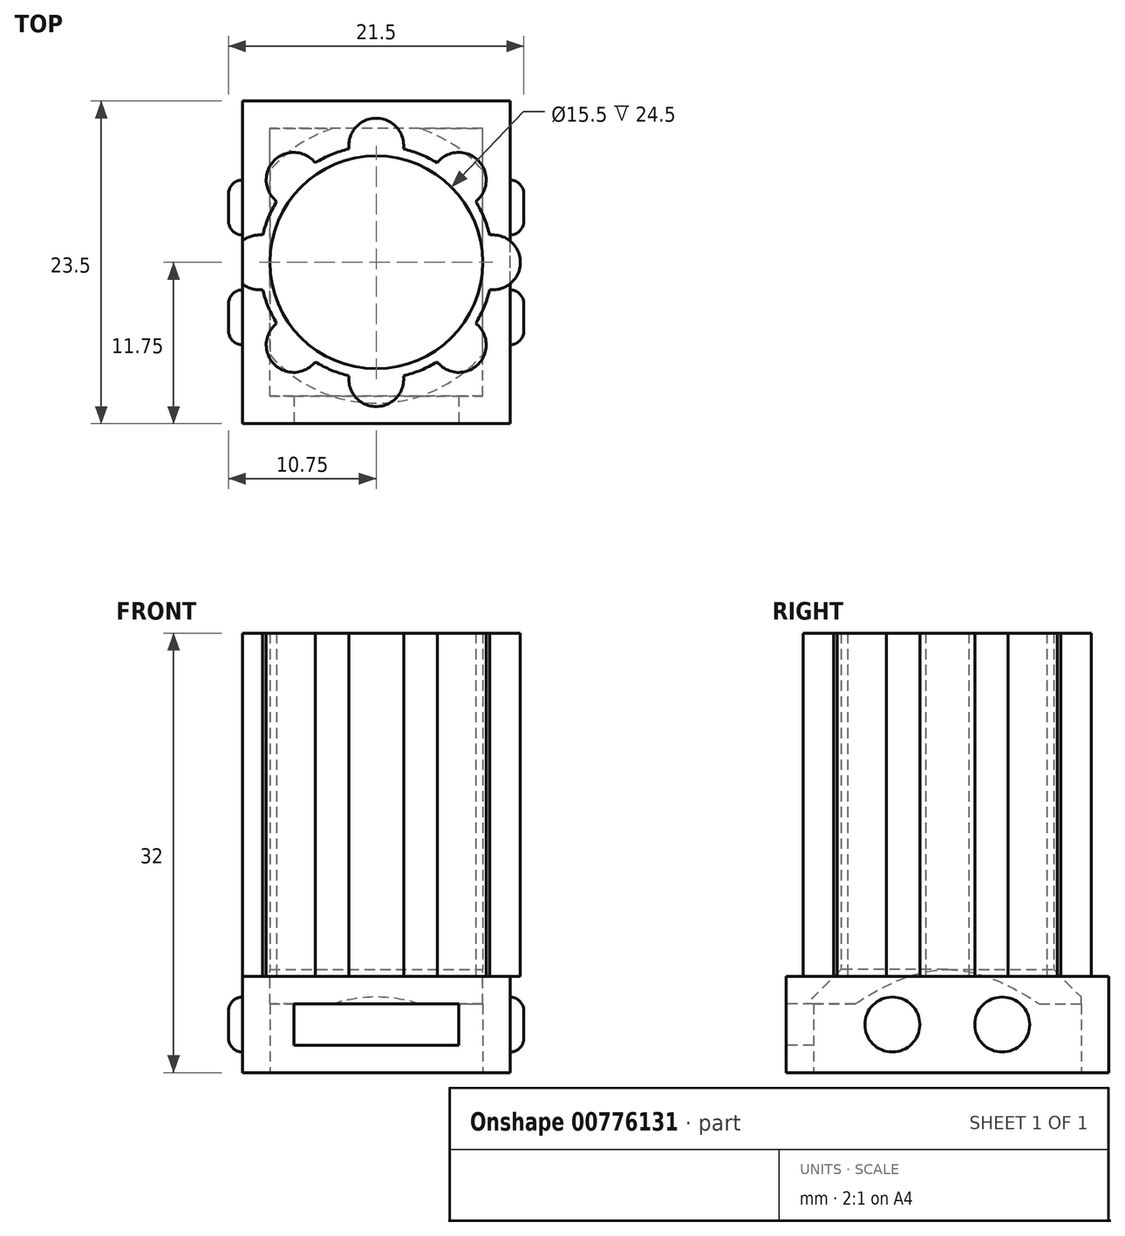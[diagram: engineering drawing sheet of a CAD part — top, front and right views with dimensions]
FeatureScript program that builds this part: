
annotation { "Feature Type Name" : "Feature", "Feature Type Description" : "" }
export const myFeature = defineFeature(function(context is Context, id is Id, definition is map)
    precondition{}
    {
        {
            var Q0;
            Q0=qCreatedBy(makeId("Top.planeOp"),FACE);
            var sketch = newSketch(context, id + "F0", { "sketchPlane" : qUnion([Q0])});
            skLineSegment(sketch, "E0.bottom", {"start": v(9.75, -11.75) * mm, "end": v(-9.75, -11.75) * mm});
            skLineSegment(sketch, "E0.top", {"start": v(9.75, 11.75) * mm, "end": v(-9.75, 11.75) * mm});
            skLineSegment(sketch, "E0.left", {"start": v(9.75, -11.75) * mm, "end": v(9.75, 11.75) * mm});
            skLineSegment(sketch, "E0.right", {"start": v(-9.75, -11.75) * mm, "end": v(-9.75, 11.75) * mm});
            skPoint(sketch, "E0.middle", {"position": v(0, 0) * mm});
            skLineSegment(sketch, "E1.bottom", {"start": v(7.75, -9.75) * mm, "end": v(-7.75, -9.75) * mm});
            skLineSegment(sketch, "E1.top", {"start": v(7.75, 9.75) * mm, "end": v(-7.75, 9.75) * mm});
            skLineSegment(sketch, "E1.left", {"start": v(7.75, -9.75) * mm, "end": v(7.75, 9.75) * mm});
            skLineSegment(sketch, "E1.right", {"start": v(-7.75, -9.75) * mm, "end": v(-7.75, 9.75) * mm});
            skSolve(sketch);
        }
        {
            var Q0;
            Q0=makeQuery(id+"F0.imprint","IMPRINT",FACE,{"disambiguationData":[TD([[makeQuery(id+"F0.imprint","IMPRINT",EDGE,{"derivedFrom":sQuery(id+"F0.wireOp",EDGE,"E0.bottom")}),-1.0]])]});
            extrude(context, id + "F1", {"entities" : qUnion([Q0]), "depth" : 7 * mm, "offsetDistance" : 25 * mm});
        }
        {
            var Q0;
            Q0=makeQuery(id+"F1.opExtrude","SWEPT_FACE",FACE,{"disambiguationData":[OSD([sQuery(id+"F0.wireOp",EDGE,"E0.left")])]});
            var sketch = newSketch(context, id + "F2", { "sketchPlane" : qUnion([Q0])});
            skPoint(sketch, "E2", {"position": v(0, 0) * mm});
            skPoint(sketch, "E3", {"position": v(0, 3.5) * mm});
            skPoint(sketch, "E4", {"position": v(4, 3.5) * mm});
            skPoint(sketch, "E5", {"position": v(-4, 3.5) * mm});
            skCircle(sketch, "E6", {"center": v(4, 3.5) * mm, "radius": 2 * mm});
            skCircle(sketch, "E7", {"center": v(-4, 3.5) * mm, "radius": 2 * mm});
            skSolve(sketch);
        }
        {
            var Q0;
            Q0=makeQuery(id+"F2.imprint","IMPRINT",FACE,{"disambiguationData":[TD([[makeQuery(id+"F2.imprint","IMPRINT",EDGE,{"derivedFrom":sQuery(id+"F2.wireOp",EDGE,"E7")}),1.0]])]});
            var Q1;
            Q1=makeQuery(id+"F2.imprint","IMPRINT",FACE,{"disambiguationData":[TD([[makeQuery(id+"F2.imprint","IMPRINT",EDGE,{"derivedFrom":sQuery(id+"F2.wireOp",EDGE,"E6")}),1.0]])]});
            extrude(context, id + "F3", {"entities" : qUnion([Q0, Q1]), "operationType" : NewBodyOperationType.ADD, "depth" : 1 * mm, "offsetDistance" : 25 * mm});
        }
        {
            var Q0;
            Q0=makeQuery(id+"F3.opExtrude","CAP_EDGE",EDGE,{"disambiguationData":[OSD([sQuery(id+"F2.wireOp",EDGE,"E6")])],"isStart":false});
            var Q1;
            Q1=makeQuery(id+"F3.opExtrude","CAP_EDGE",EDGE,{"disambiguationData":[OSD([sQuery(id+"F2.wireOp",EDGE,"E7")])],"isStart":false});
            fillet(context, id + "F4", {"entities" : qUnion([Q0, Q1]), "radius" : 1 * mm, "tangentPropagation" : true, "allowEdgeOverflow" : false});
        }
        {
            var Q0;
            Q0=makeQuery(id+"F1.opExtrude","SWEPT_FACE",FACE,{"disambiguationData":[OSD([sQuery(id+"F0.wireOp",EDGE,"E0.right")])]});
            var sketch = newSketch(context, id + "F5", { "sketchPlane" : qUnion([Q0])});
            skPoint(sketch, "E8", {"position": v(0, 0) * mm});
            skPoint(sketch, "E9", {"position": v(0, 3.5) * mm});
            skPoint(sketch, "E10", {"position": v(4, 3.5) * mm});
            skPoint(sketch, "E11", {"position": v(-4, 3.5) * mm});
            skCircle(sketch, "E12", {"center": v(4, 3.5) * mm, "radius": 2 * mm});
            skCircle(sketch, "E13", {"center": v(-4, 3.5) * mm, "radius": 2 * mm});
            skSolve(sketch);
        }
        {
            var Q0;
            Q0=makeQuery(id+"F5.imprint","IMPRINT",FACE,{"disambiguationData":[TD([[makeQuery(id+"F5.imprint","IMPRINT",EDGE,{"derivedFrom":sQuery(id+"F5.wireOp",EDGE,"E12")}),1.0]])]});
            var Q1;
            Q1=makeQuery(id+"F5.imprint","IMPRINT",FACE,{"disambiguationData":[TD([[makeQuery(id+"F5.imprint","IMPRINT",EDGE,{"derivedFrom":sQuery(id+"F5.wireOp",EDGE,"E13")}),1.0]])]});
            extrude(context, id + "F6", {"entities" : qUnion([Q0, Q1]), "operationType" : NewBodyOperationType.ADD, "depth" : 1 * mm, "offsetDistance" : 25 * mm});
        }
        {
            var Q0;
            Q0=makeQuery(id+"F6.opExtrude","CAP_EDGE",EDGE,{"disambiguationData":[OSD([sQuery(id+"F5.wireOp",EDGE,"E12")])],"isStart":false});
            var Q1;
            Q1=makeQuery(id+"F6.opExtrude","CAP_EDGE",EDGE,{"disambiguationData":[OSD([sQuery(id+"F5.wireOp",EDGE,"E13")])],"isStart":false});
            fillet(context, id + "F7", {"entities" : qUnion([Q0, Q1]), "radius" : 1 * mm, "tangentPropagation" : true, "allowEdgeOverflow" : false});
        }
        {
            var Q0;
            Q0=makeQuery(id+"F1.opExtrude","SWEPT_FACE",FACE,{"disambiguationData":[OSD([sQuery(id+"F0.wireOp",EDGE,"E1.top")])]});
            var sketch = newSketch(context, id + "F8", { "sketchPlane" : qUnion([Q0])});
            skLineSegment(sketch, "E14.bottom", {"start": v(-7.75, 7) * mm, "end": v(7.75, 7) * mm});
            skLineSegment(sketch, "E14.top", {"start": v(-7.75, 5) * mm, "end": v(7.75, 5) * mm});
            skLineSegment(sketch, "E14.left", {"start": v(-7.75, 7) * mm, "end": v(-7.75, 5) * mm});
            skLineSegment(sketch, "E14.right", {"start": v(7.75, 7) * mm, "end": v(7.75, 5) * mm});
            skSolve(sketch);
        }
        {
            var Q0;
            Q0=makeQuery(id+"F8.imprint","IMPRINT",FACE,{"disambiguationData":[TD([[makeQuery(id+"F8.imprint","IMPRINT",EDGE,{"derivedFrom":sQuery(id+"F8.wireOp",EDGE,"E14.bottom")}),1.0]])]});
            extrude(context, id + "F9", {"entities" : qUnion([Q0]), "operationType" : NewBodyOperationType.ADD, "endBound" : BoundingType.UP_TO_NEXT, "depth" : 25 * mm, "offsetDistance" : 25 * mm});
        }
        {
            var Q0;
            Q0=makeQuery(id+"F9.boolean.opBoolean","MERGE",FACE,{"derivedFrom":[makeQuery(id+"F1.opExtrude","CAP_FACE",FACE,{"disambiguationData":[OSD([sQuery(id+"F0.wireOp",EDGE,"E0.bottom"),sQuery(id+"F0.wireOp",EDGE,"E0.top"),sQuery(id+"F0.wireOp",EDGE,"E0.left"),sQuery(id+"F0.wireOp",EDGE,"E0.right"),sQuery(id+"F0.wireOp",EDGE,"E1.bottom"),sQuery(id+"F0.wireOp",EDGE,"E1.top"),sQuery(id+"F0.wireOp",EDGE,"E1.left"),sQuery(id+"F0.wireOp",EDGE,"E1.right")])],"isStart":false}),makeQuery(id+"F9.opExtrude","SWEPT_FACE",FACE,{"disambiguationData":[OSD([sQuery(id+"F8.wireOp",EDGE,"E14.bottom")])]})]});
            var sketch = newSketch(context, id + "F10", { "sketchPlane" : qUnion([Q0])});
            skCircle(sketch, "E15", {"center": v(0, 0) * mm, "radius": 8.5 * mm});
            skCircle(sketch, "E16", {"center": v(0, 8.5) * mm, "radius": 2 * mm});
            skCircle(sketch, "E17.1.0", {"center": v(-6.01, 6.01) * mm, "radius": 2 * mm});
            skCircle(sketch, "E17.2.0", {"center": v(-8.5, 0) * mm, "radius": 2 * mm});
            skCircle(sketch, "E17.3.0", {"center": v(-6.01, -6.01) * mm, "radius": 2 * mm});
            skCircle(sketch, "E17.4.0", {"center": v(0, -8.5) * mm, "radius": 2 * mm});
            skCircle(sketch, "E17.5.0", {"center": v(6.01, -6.01) * mm, "radius": 2 * mm});
            skCircle(sketch, "E17.6.0", {"center": v(8.5, 0) * mm, "radius": 2 * mm});
            skCircle(sketch, "E17.7.0", {"center": v(6.01, 6.01) * mm, "radius": 2 * mm});
            skSolve(sketch);
        }
        {
            var Q0;
            {var subQ1=sQuery(id+"F10.wireOp",EDGE,"E15");var subQ20=sQuery(id+"F10.wireOp",EDGE,"E17.7.0");var subQ21=makeQuery(id+"F10.imprint","INTERSECT",VERTEX,{"disambiguationData":[OD(0.0)],"derivedFrom":[subQ1,subQ20]});Q0=makeQuery(id+"F10.imprint","IMPRINT",FACE,{"disambiguationData":[TD([[makeQuery(id+"F10.imprint","IMPRINT",EDGE,{"disambiguationData":[TD([[subQ21,1.0]])],"derivedFrom":subQ1}),1.0]])]});}
            var Q1;
            {var subQ0=sQuery(id+"F10.wireOp",EDGE,"E17.4.0");var subQ1=sQuery(id+"F10.wireOp",EDGE,"E15");var subQ2=makeQuery(id+"F10.imprint","INTERSECT",VERTEX,{"disambiguationData":[OD(0.0)],"derivedFrom":[subQ1,subQ0]});Q1=makeQuery(id+"F10.imprint","IMPRINT",FACE,{"disambiguationData":[TD([[makeQuery(id+"F10.imprint","IMPRINT",EDGE,{"disambiguationData":[TD([[subQ2,-1.0]])],"derivedFrom":subQ1}),1.0]])]});}
            var Q2;
            {var subQ0=sQuery(id+"F10.wireOp",EDGE,"E17.4.0");var subQ1=sQuery(id+"F10.wireOp",EDGE,"E15");var subQ2=makeQuery(id+"F10.imprint","INTERSECT",VERTEX,{"disambiguationData":[OD(0.0)],"derivedFrom":[subQ1,subQ0]});Q2=makeQuery(id+"F10.imprint","IMPRINT",FACE,{"disambiguationData":[TD([[makeQuery(id+"F10.imprint","IMPRINT",EDGE,{"disambiguationData":[TD([[subQ2,-1.0]])],"derivedFrom":subQ1}),-1.0]])]});}
            var Q3;
            {var subQ0=sQuery(id+"F10.wireOp",EDGE,"E17.5.0");var subQ1=sQuery(id+"F10.wireOp",EDGE,"E15");var subQ2=makeQuery(id+"F10.imprint","INTERSECT",VERTEX,{"disambiguationData":[OD(0.0)],"derivedFrom":[subQ1,subQ0]});Q3=makeQuery(id+"F10.imprint","IMPRINT",FACE,{"disambiguationData":[TD([[makeQuery(id+"F10.imprint","IMPRINT",EDGE,{"disambiguationData":[TD([[subQ2,-1.0]])],"derivedFrom":subQ1}),1.0]])]});}
            var Q4;
            {var subQ0=sQuery(id+"F10.wireOp",EDGE,"E17.5.0");var subQ1=sQuery(id+"F10.wireOp",EDGE,"E15");var subQ2=makeQuery(id+"F10.imprint","INTERSECT",VERTEX,{"disambiguationData":[OD(0.0)],"derivedFrom":[subQ1,subQ0]});Q4=makeQuery(id+"F10.imprint","IMPRINT",FACE,{"disambiguationData":[TD([[makeQuery(id+"F10.imprint","IMPRINT",EDGE,{"disambiguationData":[TD([[subQ2,-1.0]])],"derivedFrom":subQ1}),-1.0]])]});}
            var Q5;
            {var subQ0=sQuery(id+"F10.wireOp",EDGE,"E17.6.0");var subQ1=sQuery(id+"F10.wireOp",EDGE,"E15");var subQ2=makeQuery(id+"F10.imprint","INTERSECT",VERTEX,{"disambiguationData":[OD(0.0)],"derivedFrom":[subQ1,subQ0]});Q5=makeQuery(id+"F10.imprint","IMPRINT",FACE,{"disambiguationData":[TD([[makeQuery(id+"F10.imprint","IMPRINT",EDGE,{"disambiguationData":[TD([[subQ2,1.0]])],"derivedFrom":subQ1}),1.0]])]});}
            var Q6;
            {var subQ0=sQuery(id+"F10.wireOp",EDGE,"E17.6.0");var subQ1=sQuery(id+"F10.wireOp",EDGE,"E15");var subQ2=makeQuery(id+"F10.imprint","INTERSECT",VERTEX,{"disambiguationData":[OD(0.0)],"derivedFrom":[subQ1,subQ0]});Q6=makeQuery(id+"F10.imprint","IMPRINT",FACE,{"disambiguationData":[TD([[makeQuery(id+"F10.imprint","IMPRINT",EDGE,{"disambiguationData":[TD([[subQ2,1.0]])],"derivedFrom":subQ1}),-1.0]])]});}
            var Q7;
            {var subQ0=sQuery(id+"F10.wireOp",EDGE,"E17.6.0");var subQ1=makeQuery(id+"F1.opExtrude","CAP_EDGE",EDGE,{"disambiguationData":[OSD([sQuery(id+"F0.wireOp",EDGE,"E0.left")])],"isStart":false});var subQ2=makeQuery(id+"F10.imprint","INTERSECT",VERTEX,{"disambiguationData":[OD(0.0)],"derivedFrom":[subQ1,subQ0]});Q7=makeQuery(id+"F10.imprint","IMPRINT",FACE,{"disambiguationData":[TD([[makeQuery(id+"F10.imprint","IMPRINT",EDGE,{"disambiguationData":[TD([[subQ2,1.0]])],"derivedFrom":subQ0}),1.0]])]});}
            var Q8;
            {var subQ0=sQuery(id+"F10.wireOp",EDGE,"E17.7.0");var subQ1=sQuery(id+"F10.wireOp",EDGE,"E15");var subQ2=makeQuery(id+"F10.imprint","INTERSECT",VERTEX,{"disambiguationData":[OD(0.0)],"derivedFrom":[subQ1,subQ0]});Q8=makeQuery(id+"F10.imprint","IMPRINT",FACE,{"disambiguationData":[TD([[makeQuery(id+"F10.imprint","IMPRINT",EDGE,{"disambiguationData":[TD([[subQ2,-1.0]])],"derivedFrom":subQ1}),1.0]])]});}
            var Q9;
            {var subQ0=sQuery(id+"F10.wireOp",EDGE,"E17.7.0");var subQ1=sQuery(id+"F10.wireOp",EDGE,"E15");var subQ2=makeQuery(id+"F10.imprint","INTERSECT",VERTEX,{"disambiguationData":[OD(0.0)],"derivedFrom":[subQ1,subQ0]});Q9=makeQuery(id+"F10.imprint","IMPRINT",FACE,{"disambiguationData":[TD([[makeQuery(id+"F10.imprint","IMPRINT",EDGE,{"disambiguationData":[TD([[subQ2,-1.0]])],"derivedFrom":subQ1}),-1.0]])]});}
            var Q10;
            {var subQ0=sQuery(id+"F10.wireOp",EDGE,"E16");var subQ1=sQuery(id+"F10.wireOp",EDGE,"E15");var subQ2=makeQuery(id+"F10.imprint","INTERSECT",VERTEX,{"disambiguationData":[OD(0.0)],"derivedFrom":[subQ1,subQ0]});Q10=makeQuery(id+"F10.imprint","IMPRINT",FACE,{"disambiguationData":[TD([[makeQuery(id+"F10.imprint","IMPRINT",EDGE,{"disambiguationData":[TD([[subQ2,-1.0]])],"derivedFrom":subQ1}),1.0]])]});}
            var Q11;
            {var subQ0=sQuery(id+"F10.wireOp",EDGE,"E16");var subQ1=sQuery(id+"F10.wireOp",EDGE,"E15");var subQ2=makeQuery(id+"F10.imprint","INTERSECT",VERTEX,{"disambiguationData":[OD(0.0)],"derivedFrom":[subQ1,subQ0]});Q11=makeQuery(id+"F10.imprint","IMPRINT",FACE,{"disambiguationData":[TD([[makeQuery(id+"F10.imprint","IMPRINT",EDGE,{"disambiguationData":[TD([[subQ2,-1.0]])],"derivedFrom":subQ1}),-1.0]])]});}
            var Q12;
            {var subQ0=sQuery(id+"F10.wireOp",EDGE,"E17.1.0");var subQ1=sQuery(id+"F10.wireOp",EDGE,"E15");var subQ2=makeQuery(id+"F10.imprint","INTERSECT",VERTEX,{"disambiguationData":[OD(0.0)],"derivedFrom":[subQ1,subQ0]});Q12=makeQuery(id+"F10.imprint","IMPRINT",FACE,{"disambiguationData":[TD([[makeQuery(id+"F10.imprint","IMPRINT",EDGE,{"disambiguationData":[TD([[subQ2,-1.0]])],"derivedFrom":subQ1}),1.0]])]});}
            var Q13;
            {var subQ0=sQuery(id+"F10.wireOp",EDGE,"E17.1.0");var subQ1=sQuery(id+"F10.wireOp",EDGE,"E15");var subQ2=makeQuery(id+"F10.imprint","INTERSECT",VERTEX,{"disambiguationData":[OD(0.0)],"derivedFrom":[subQ1,subQ0]});Q13=makeQuery(id+"F10.imprint","IMPRINT",FACE,{"disambiguationData":[TD([[makeQuery(id+"F10.imprint","IMPRINT",EDGE,{"disambiguationData":[TD([[subQ2,-1.0]])],"derivedFrom":subQ1}),-1.0]])]});}
            var Q14;
            {var subQ0=sQuery(id+"F10.wireOp",EDGE,"E17.2.0");var subQ1=sQuery(id+"F10.wireOp",EDGE,"E15");var subQ2=makeQuery(id+"F10.imprint","INTERSECT",VERTEX,{"disambiguationData":[OD(0.0)],"derivedFrom":[subQ1,subQ0]});Q14=makeQuery(id+"F10.imprint","IMPRINT",FACE,{"disambiguationData":[TD([[makeQuery(id+"F10.imprint","IMPRINT",EDGE,{"disambiguationData":[TD([[subQ2,-1.0]])],"derivedFrom":subQ1}),1.0]])]});}
            var Q15;
            {var subQ0=sQuery(id+"F10.wireOp",EDGE,"E17.2.0");var subQ1=sQuery(id+"F10.wireOp",EDGE,"E15");var subQ2=makeQuery(id+"F10.imprint","INTERSECT",VERTEX,{"disambiguationData":[OD(0.0)],"derivedFrom":[subQ1,subQ0]});Q15=makeQuery(id+"F10.imprint","IMPRINT",FACE,{"disambiguationData":[TD([[makeQuery(id+"F10.imprint","IMPRINT",EDGE,{"disambiguationData":[TD([[subQ2,-1.0]])],"derivedFrom":subQ1}),-1.0]])]});}
            var Q16;
            {var subQ0=sQuery(id+"F10.wireOp",EDGE,"E17.2.0");var subQ1=makeQuery(id+"F1.opExtrude","CAP_EDGE",EDGE,{"disambiguationData":[OSD([sQuery(id+"F0.wireOp",EDGE,"E0.right")])],"isStart":false});var subQ2=makeQuery(id+"F10.imprint","INTERSECT",VERTEX,{"disambiguationData":[OD(0.0)],"derivedFrom":[subQ1,subQ0]});Q16=makeQuery(id+"F10.imprint","IMPRINT",FACE,{"disambiguationData":[TD([[makeQuery(id+"F10.imprint","IMPRINT",EDGE,{"disambiguationData":[TD([[subQ2,1.0]])],"derivedFrom":subQ0}),1.0]])]});}
            var Q17;
            {var subQ0=sQuery(id+"F10.wireOp",EDGE,"E17.3.0");var subQ1=sQuery(id+"F10.wireOp",EDGE,"E15");var subQ2=makeQuery(id+"F10.imprint","INTERSECT",VERTEX,{"disambiguationData":[OD(0.0)],"derivedFrom":[subQ1,subQ0]});Q17=makeQuery(id+"F10.imprint","IMPRINT",FACE,{"disambiguationData":[TD([[makeQuery(id+"F10.imprint","IMPRINT",EDGE,{"disambiguationData":[TD([[subQ2,-1.0]])],"derivedFrom":subQ1}),1.0]])]});}
            var Q18;
            {var subQ0=sQuery(id+"F10.wireOp",EDGE,"E17.3.0");var subQ1=sQuery(id+"F10.wireOp",EDGE,"E15");var subQ2=makeQuery(id+"F10.imprint","INTERSECT",VERTEX,{"disambiguationData":[OD(0.0)],"derivedFrom":[subQ1,subQ0]});Q18=makeQuery(id+"F10.imprint","IMPRINT",FACE,{"disambiguationData":[TD([[makeQuery(id+"F10.imprint","IMPRINT",EDGE,{"disambiguationData":[TD([[subQ2,-1.0]])],"derivedFrom":subQ1}),-1.0]])]});}
            extrude(context, id + "F11", {"entities" : qUnion([Q0, Q1, Q2, Q3, Q4, Q5, Q6, Q7, Q8, Q9, Q10, Q11, Q12, Q13, Q14, Q15, Q16, Q17, Q18]), "operationType" : NewBodyOperationType.ADD, "depth" : 25 * mm, "offsetDistance" : 25 * mm});
        }
        {
            var Q0;
            Q0=makeQuery(id+"F9.opExtrude","SWEPT_FACE",FACE,{"disambiguationData":[OSD([sQuery(id+"F8.wireOp",EDGE,"E14.top")])]});
            var sketch = newSketch(context, id + "F12", { "sketchPlane" : qUnion([Q0])});
            skCircle(sketch, "E18", {"center": v(0, 0) * mm, "radius": 7.75 * mm});
            skSolve(sketch);
        }
        {
            var Q0;
            {var subQ0=sQuery(id+"F12.wireOp",EDGE,"E18");var subQ1=sQuery(id+"F8.wireOp",EDGE,"E14.top");var subQ2=sQuery(id+"F0.wireOp",EDGE,"E1.top");var subQ3=makeQuery(id+"F12.imprint","INTERSECT",VERTEX,{"derivedFrom":[makeQuery(id+"F9.opExtrude","SWEPT_EDGE",EDGE,{"disambiguationData":[OSD([subQ2,sQuery(id+"F0.wireOp",EDGE,"E1.right"),subQ1,sQuery(id+"F8.wireOp",EDGE,"E14.left")])]}),subQ0]});Q0=makeQuery(id+"F12.imprint","IMPRINT",FACE,{"disambiguationData":[TD([[makeQuery(id+"F12.imprint","IMPRINT",EDGE,{"disambiguationData":[TD([[subQ3,1.0]])],"derivedFrom":subQ0}),1.0]])]});}
            extrude(context, id + "F13", {"entities" : qUnion([Q0]), "operationType" : NewBodyOperationType.REMOVE, "endBound" : BoundingType.UP_TO_NEXT, "oppositeDirection" : true, "depth" : 25 * mm, "offsetDistance" : 25 * mm});
        }
        {
            var Q0;
            Q0=makeQuery(id+"F1.opExtrude","SWEPT_FACE",FACE,{"disambiguationData":[OSD([sQuery(id+"F0.wireOp",EDGE,"E0.bottom")])]});
            var sketch = newSketch(context, id + "F14", { "sketchPlane" : qUnion([Q0])});
            skLineSegment(sketch, "E19.bottom", {"start": v(6, 2) * mm, "end": v(-6, 2) * mm});
            skLineSegment(sketch, "E19.top", {"start": v(6, 5) * mm, "end": v(-6, 5) * mm});
            skLineSegment(sketch, "E19.left", {"start": v(6, 2) * mm, "end": v(6, 5) * mm});
            skLineSegment(sketch, "E19.right", {"start": v(-6, 2) * mm, "end": v(-6, 5) * mm});
            skPoint(sketch, "E19.middle", {"position": v(0, 3.5) * mm});
            skPoint(sketch, "E19.middle.positionSnap0", {"position": v(0, 0) * mm});
            skPoint(sketch, "E19.centerSnap0", {"position": v(0, 0) * mm});
            skSolve(sketch);
        }
        {
            var Q0;
            Q0=makeQuery(id+"F14.imprint","IMPRINT",FACE,{"disambiguationData":[TD([[makeQuery(id+"F14.imprint","IMPRINT",EDGE,{"derivedFrom":sQuery(id+"F14.wireOp",EDGE,"E19.bottom")}),-1.0]])]});
            extrude(context, id + "F15", {"entities" : qUnion([Q0]), "operationType" : NewBodyOperationType.REMOVE, "endBound" : BoundingType.UP_TO_NEXT, "oppositeDirection" : true, "depth" : 25 * mm, "offsetDistance" : 25 * mm});
        }
        {
            var Q0;
            Q0=makeQuery(id+"F13.boolean.opBoolean","COPY",EDGE,{"disambiguationData":[OD(0.0)],"derivedFrom":makeQuery(id+"F13.opExtrude","CAP_EDGE",EDGE,{"disambiguationData":[OSD([sQuery(id+"F12.wireOp",EDGE,"E18")])],"isStart":true})});
            chamfer(context, id + "F16", {"entities" : qUnion([Q0]), "chamferType" : ChamferType.TWO_OFFSETS, "width1" : 2.5 * mm, "oppositeDirection" : false, "width2" : 2.5 * mm, "tangentPropagation" : true});
        }
    });
